FCSTD DOCUMENT  (FreeCAD 1.0R39319 (Git))
Label: Week2Sketch2
License: All rights reserved
LicenseURL: https://en.wikipedia.org/wiki/All_rights_reserved
objects: Spreadsheet::Sheet×1, Sketcher::SketchObject×1, PartDesign::Body×1
note: 3 computed .brp shape members not serialized (recipe doc carries the construction recipe); baked Part::Feature solids carry a one-line shape summary decoded from their .brp

FEATURE [Spreadsheet::Sheet] Spreadsheet
  cells = A1='y_totaldis; B1(y_totaldis)=75; A2='y_rside_max_dis; B2(y_rside_max_dis)=57; A3='right_side_box; B3(right_side_box)=4; A4='y_from_box_to_top; B4(y_from_box_to_top)=14; A5='x_fromrtoptoleft; B5(x_fromrtoptoleft)=18; A6='x_centertop_dis; B6(x_centertop_dis)=22; A7='x_center_box; B7(x_center_box)=8; A8='y_center_box; B8(y_center_box)=4; A9='slant_top_left_dis; B9(slant_top_left_dis)=3; A10='x_dis_from_slant_to_left; B10(x_dis_from_slant_to_left)=21; A11='left_rid ; B11(left_rid)=5; A12='x_disfromlefttoright; B12(x_disfromlefttoright)=5; A13='y_disleftbottom; B13(y_disleftbottom)=10; A14='y_centerdis ; B14(y_centerdis)=22; A15='y_rightbottom; B15(y_rightbottom)=15; A16='x_dis_centerbottom; B16(x_dis_centerbottom)=21; A17='x_dis_rightbottom; B17(x_dis_rightbottom)=17; A18='y_dis_centerbttom; B18(y_dis_centerbttom)=22; A19='x_leftbottom_notch; B19(x_leftbottom_notch)=4; A20='Radius_inner_gear; B20(Radius_inner_gear)=6.4; A21='radius_outer_gear; B21(radius_outer_gear)=8.5; A22='radius_gear; B22(radius_gear)=2.2
FEATURE [Sketcher::SketchObject] Sketch
  ArcFitTolerance = 1e-06
  AttachmentSupport = -> [XY_Plane]
  FullyConstrained = false
  MakeInternals = false
  MapMode = 5
  expr: Constraints[12] = <<Spreadsheet>>.right_side_box
  expr: Constraints[13] = <<Spreadsheet>>.right_side_box
  expr: Constraints[14] = <<Spreadsheet>>.y_from_box_to_top
  expr: Constraints[29] = <<Spreadsheet>>.x_fromrtoptoleft
  expr: Constraints[2] = <<Spreadsheet>>.y_rside_max_dis
  expr: Constraints[30] = <<Spreadsheet>>.y_from_box_to_top + <<Spreadsheet>>.right_side_box
  expr: Constraints[33] = <<Spreadsheet>>.x_centertop_dis
  expr: Constraints[35] = <<Spreadsheet>>.x_center_box
  expr: Constraints[36] = <<Spreadsheet>>.y_center_box
  expr: Constraints[37] = <<Spreadsheet>>.y_from_box_to_top + <<Spreadsheet>>.right_side_box
  expr: Constraints[69] = <<Spreadsheet>>.y_totaldis
  expr: Constraints[70] = <<Spreadsheet>>.slant_top_left_dis
  expr: Constraints[71] = <<Spreadsheet>>.left_rid
  expr: Constraints[72] = <<Spreadsheet>>.x_dis_rightbottom
  expr: Constraints[73] = <<Spreadsheet>>.y_rightbottom
  expr: Constraints[74] = <<Spreadsheet>>.x_dis_centerbottom
  expr: Constraints[75] = <<Spreadsheet>>.y_dis_centerbttom
  expr: Constraints[76] = <<Spreadsheet>>.x_leftbottom_notch
  expr: Constraints[77] = <<Spreadsheet>>.y_disleftbottom
  expr: Constraints[82] = <<Spreadsheet>>.x_dis_from_slant_to_left
  expr: Constraints[83] = <<Spreadsheet>>.x_disfromlefttoright
  expr: Constraints[93] = <<Spreadsheet>>.radius_outer_gear
  expr: Constraints[95] = <<Spreadsheet>>.Radius_inner_gear
  sketch-geometry (55):
    g0: LineSegment StartX=0 StartY=0 StartZ=0 EndX=0 EndY=57 EndZ=0
    g1: LineSegment StartX=0 StartY=57 StartZ=0 EndX=-4 EndY=57 EndZ=0
    g2: LineSegment StartX=-4 StartY=57 StartZ=0 EndX=-4 EndY=61 EndZ=0
    g3: LineSegment StartX=-4 StartY=61 StartZ=0 EndX=0 EndY=61 EndZ=0
    g4: LineSegment StartX=0 StartY=61 StartZ=0 EndX=0 EndY=75 EndZ=0
    g5: LineSegment StartX=0 StartY=75 StartZ=0 EndX=-18 EndY=75 EndZ=0
    g6: LineSegment StartX=-18 StartY=75 StartZ=0 EndX=-18 EndY=57 EndZ=0
    g7: LineSegment StartX=-18 StartY=57 StartZ=0 EndX=-25 EndY=57 EndZ=0
    g8: LineSegment StartX=-25 StartY=57 StartZ=0 EndX=-25 EndY=53 EndZ=0
    g9: LineSegment StartX=-25 StartY=53 StartZ=0 EndX=-33 EndY=53 EndZ=0
    g10: LineSegment StartX=-33 StartY=53 StartZ=0 EndX=-33 EndY=57 EndZ=0
    g11: LineSegment StartX=-33 StartY=57 StartZ=0 EndX=-40 EndY=57 EndZ=0
    g12: LineSegment StartX=-40 StartY=57 StartZ=0 EndX=-40 EndY=73.4506 EndZ=0
    g13: LineSegment StartX=0 StartY=0 StartZ=0 EndX=-17 EndY=0 EndZ=0
    g14: LineSegment StartX=-17 StartY=0 StartZ=0 EndX=-17 EndY=15 EndZ=0
    g15: LineSegment StartX=-17 StartY=15 StartZ=0 EndX=-38 EndY=15 EndZ=0
    g16: LineSegment StartX=-38 StartY=15 StartZ=0 EndX=-38 EndY=37 EndZ=0
    g17: LineSegment StartX=-38 StartY=37 StartZ=0 EndX=-42 EndY=37 EndZ=0
    g18: LineSegment StartX=-42 StartY=37 StartZ=0 EndX=-42 EndY=27 EndZ=0
    g19: LineSegment StartX=-42 StartY=27 StartZ=0 EndX=-46 EndY=27 EndZ=0
    g20: LineSegment StartX=-46 StartY=27 StartZ=0 EndX=-46 EndY=32 EndZ=0
    g21: LineSegment StartX=-46 StartY=32 StartZ=0 EndX=-50 EndY=32 EndZ=0
    g22: LineSegment StartX=-50 StartY=32 StartZ=0 EndX=-50 EndY=27 EndZ=0
    g23: LineSegment StartX=-50 StartY=27 StartZ=0 EndX=-54 EndY=27 EndZ=0
    g24: LineSegment StartX=-54 StartY=27 StartZ=0 EndX=-54 EndY=37 EndZ=0
    g25: LineSegment StartX=-54 StartY=37 StartZ=0 EndX=-59 EndY=37 EndZ=0
    g26: LineSegment StartX=-59 StartY=37 StartZ=0 EndX=-59 EndY=61 EndZ=0
    g27: ArcOfCircle CenterX=-54 CenterY=61 CenterZ=0 NormalX=0 NormalY=0 NormalZ=1 AngleXU=0 Radius=5 StartAngle=2.17657 EndAngle=3.14159
    g28: LineSegment StartX=-56.847 StartY=65.1103 StartZ=0 EndX=-42.5689 EndY=75 EndZ=0
    g29: LineSegment StartX=-42.5689 StartY=75 StartZ=0 EndX=-40 EndY=73.4506 EndZ=0
    g30: GeomPoint X=-54 Y=32 Z=0
    g31: LineSegment [constr] StartX=-38 StartY=37 StartZ=0 EndX=-17 EndY=37 EndZ=0
    g32: LineSegment [constr] StartX=-17 StartY=15 StartZ=0 EndX=-17 EndY=37 EndZ=0
    g33: ArcOfCircle CenterX=-17 CenterY=37 CenterZ=0 NormalX=0 NormalY=0 NormalZ=1 AngleXU=0 Radius=4.25 StartAngle=2.11632 EndAngle=2.25889
    g34: Circle [constr] CenterX=-17 CenterY=37 CenterZ=0 NormalX=0 NormalY=0 NormalZ=1 AngleXU=0 Radius=3.2
    g35: ArcOfCircle CenterX=-21.25 CenterY=37 CenterZ=0 NormalX=0 NormalY=0 NormalZ=1 AngleXU=0 Radius=1.05 StartAngle=4.83623 EndAngle=7.73014
    g36: ArcOfCircle CenterX=-20.4215 CenterY=39.521 CenterZ=0 NormalX=0 NormalY=0 NormalZ=1 AngleXU=0 Radius=1.05 StartAngle=4.20123 EndAngle=7.09513
    g37: ArcOfCircle CenterX=-18.2472 CenterY=41.0629 CenterZ=0 NormalX=0 NormalY=0 NormalZ=1 AngleXU=0 Radius=1.05 StartAngle=3.56327 EndAngle=6.45717
    g38: ArcOfCircle CenterX=-15.6866 CenterY=41.042 CenterZ=0 NormalX=0 NormalY=0 NormalZ=1 AngleXU=0 Radius=1.05 StartAngle=2.95125 EndAngle=5.84515
    g39: ArcOfCircle CenterX=-13.592 CenterY=39.5393 CenterZ=0 NormalX=0 NormalY=0 NormalZ=1 AngleXU=0 Radius=1.05 StartAngle=2.335 EndAngle=5.2289
    g40: ArcOfCircle CenterX=-12.7505 CenterY=37.0661 CenterZ=0 NormalX=0 NormalY=0 NormalZ=1 AngleXU=0 Radius=1.05 StartAngle=1.7102 EndAngle=4.6041
    g41: ArcOfCircle CenterX=-13.5156 CenterY=34.5666 CenterZ=0 NormalX=0 NormalY=0 NormalZ=1 AngleXU=0 Radius=1.05 StartAngle=1.08501 EndAngle=3.97891
    g42: ArcOfCircle CenterX=-15.5707 CenterY=32.9976 CenterZ=0 NormalX=0 NormalY=0 NormalZ=1 AngleXU=0 Radius=1.05 StartAngle=0.46684 EndAngle=3.36074
    g43: ArcOfCircle CenterX=-18.329 CenterY=32.9631 CenterZ=0 NormalX=0 NormalY=0 NormalZ=1 AngleXU=0 Radius=1.05 StartAngle=6.089 EndAngle=8.9829
    g44: ArcOfCircle CenterX=-20.3699 CenterY=34.4104 CenterZ=0 NormalX=0 NormalY=0 NormalZ=1 AngleXU=0 Radius=1.05 StartAngle=5.49145 EndAngle=8.38535
    g45: ArcOfCircle CenterX=-21.25 CenterY=37 CenterZ=0 NormalX=0 NormalY=0 NormalZ=1 AngleXU=0 Radius=1.05 StartAngle=4.83624 EndAngle=7.73014
    g46: ArcOfCircle CenterX=-17 CenterY=37 CenterZ=0 NormalX=0 NormalY=0 NormalZ=1 AngleXU=0 Radius=4.25 StartAngle=1.5043 EndAngle=1.62094
    g47: ArcOfCircle CenterX=-17 CenterY=37 CenterZ=0 NormalX=0 NormalY=0 NormalZ=1 AngleXU=0 Radius=4.25 StartAngle=0.888051 EndAngle=1.00892
    g48: ArcOfCircle CenterX=-17 CenterY=37 CenterZ=0 NormalX=0 NormalY=0 NormalZ=1 AngleXU=0 Radius=4.25 StartAngle=0.263249 EndAngle=0.392668
    g49: ArcOfCircle CenterX=-17 CenterY=37 CenterZ=0 NormalX=0 NormalY=0 NormalZ=1 AngleXU=0 Radius=4.25 StartAngle=5.92124 EndAngle=6.05105
    g50: ArcOfCircle CenterX=-17 CenterY=37 CenterZ=0 NormalX=0 NormalY=0 NormalZ=1 AngleXU=0 Radius=4.25 StartAngle=5.30307 EndAngle=5.42586
    g51: ArcOfCircle CenterX=-17 CenterY=37 CenterZ=0 NormalX=0 NormalY=0 NormalZ=1 AngleXU=0 Radius=4.25 StartAngle=4.64205 EndAngle=4.80769
    g52: ArcOfCircle CenterX=-17 CenterY=37 CenterZ=0 NormalX=0 NormalY=0 NormalZ=1 AngleXU=0 Radius=4.25 StartAngle=4.0445 EndAngle=4.14666
    g53: ArcOfCircle CenterX=-17 CenterY=37 CenterZ=0 NormalX=0 NormalY=0 NormalZ=1 AngleXU=0 Radius=4.25 StartAngle=3.38928 EndAngle=3.54911
    g54: ArcOfCircle CenterX=-17 CenterY=37 CenterZ=0 NormalX=0 NormalY=0 NormalZ=1 AngleXU=0 Radius=4.25 StartAngle=2.75427 EndAngle=2.8939
  constraints (160):
    c: Coincident(g0,g-1)
    c: PointOnObject(g0,g-2)
    c: DistanceY(g0,g0) = 57
    c: Coincident(g0,g1)
    c: Horizontal(g1)
    c: Coincident(g1,g2)
    c: Vertical(g2)
    c: Coincident(g2,g3)
    c: PointOnObject(g3,g-2)
    c: Horizontal(g3)
    c: Coincident(g3,g4)
    c: PointOnObject(g4,g-2)
    c: Distance(g1,g1) = 4
    c: DistanceY(g2,g2) = 4
    c: DistanceY(g4,g4) = 14
    c: Coincident(g4,g5)
    c: Horizontal(g5)
    c: Coincident(g5,g6)
    c: Vertical(g6)
    c: Coincident(g6,g7)
    c: Horizontal(g7)
    c: Coincident(g7,g8)
    c: Vertical(g8)
    c: Coincident(g8,g9)
    c: Horizontal(g9)
    c: Coincident(g9,g10)
    c: Vertical(g10)
    c: Coincident(g10,g11)
    c: Horizontal(g11)
    c: DistanceX(g5,g5) = 18
    c: DistanceY(g6,g6) = 18
    c: Coincident(g12,g11)
    c: Vertical(g12)
    c: Distance(g12,g6) = 22
    c: Equal(g7,g11)
    c: DistanceX(g9,g9) = 8
    c: Distance(g11,g9) = 4
    c: Distance(g11,g5) = 18
    c: Coincident(g0,g13)
    c: PointOnObject(g13,g-1)
    c: Coincident(g13,g14)
    c: Vertical(g14)
    c: Coincident(g14,g15)
    c: Horizontal(g15)
    c: Coincident(g15,g16)
    c: Vertical(g16)
    c: Coincident(g16,g17)
    c: Horizontal(g17)
    c: Coincident(g17,g18)
    c: Vertical(g18)
    c: Coincident(g18,g19)
    c: Horizontal(g19)
    c: Coincident(g19,g20)
    c: Coincident(g20,g21)
    c: Horizontal(g21)
    c: Coincident(g21,g22)
    c: Vertical(g22)
    c: Coincident(g22,g23)
    c: Horizontal(g23)
    c: Coincident(g23,g24)
    c: Vertical(g24)
    c: Coincident(g24,g25)
    c: Horizontal(g25)
    c: Coincident(g25,g26)
    c: Vertical(g26)
    c: Tangent(g26,g27) = 1.5708
    c: Tangent(g27,g28) = 1.5708
    c: Coincident(g28,g29)
    c: Coincident(g29,g12)
    c: Distance(g28,g13) = 75
    c: Distance(g29,g29) = 3
    c: Radius(g27) = 5
    c: DistanceX(g13,g13) = 17
    c: DistanceY(g14,g14) = 15
    c: DistanceX(g15,g15) = 21
    c: DistanceY(g16,g16) = 22
    c: Distance(g17,g17) = 4
    c: DistanceY(g18,g18) = 10
    c: Vertical(g20)
    c: Equal(g18,g24)
    c: Equal(g23,g21)
    c: Equal(g21,g19)
    c: Distance(g26,g16) = 21
    c: Distance(g25,g25) = 5
    c: Equal(g20,g22)
    c: Symmetric(g24,g24,g30)
    c: Horizontal(g21,g30)
    c: Coincident(g31,g16)
    c: Horizontal(g31)
    c: Coincident(g32,g14)
    c: Vertical(g32)
    c: Coincident(g31,g32)
    c: Coincident(g33,g31)
    c: Diameter(g33) = 8.5
    c: Coincident(g34,g31)
    c: Diameter(g34) = 6.4
    c: Block(g32)
    c: Block(g31)
    c: PointOnObject(g35,g31)
    c: Tangent(g35,g34)
    c: PointOnObject(g35,g53)
    c: PointOnObject(g35,g54)
    c: PointOnObject(g36,g54)
    c: PointOnObject(g36,g33)
    c: PointOnObject(g37,g33)
    c: PointOnObject(g38,g46)
    c: PointOnObject(g38,g33)
    c: PointOnObject(g39,g47)
    c: PointOnObject(g39,g33)
    c: PointOnObject(g40,g48)
    c: PointOnObject(g40,g33)
    c: PointOnObject(g41,g49)
    c: PointOnObject(g41,g33)
    c: PointOnObject(g42,g50)
    c: PointOnObject(g42,g51)
    c: PointOnObject(g43,g51)
    c: PointOnObject(g43,g52)
    c: PointOnObject(g44,g52)
    c: PointOnObject(g44,g53)
    c: Equal(g35, g36-g44) x9
    c: Coincident(g46,g37)
    c: Coincident(g33,g37)
    c: Equal(g33,g46)
    c: Coincident(g47,g38)
    c: PointOnObject(g46,g38)
    c: Coincident(g33,g46)
    c: Equal(g33,g47)
    c: Coincident(g48,g39)
    c: PointOnObject(g47,g39)
    c: Coincident(g33,g47)
    c: Equal(g33,g48)
    c: Coincident(g49,g40)
    c: PointOnObject(g48,g40)
    c: Coincident(g33,g48)
    c: Equal(g33,g49)
    c: Coincident(g50,g41)
    c: PointOnObject(g49,g41)
    c: Coincident(g33,g49)
    c: Equal(g33,g50)
    c: Coincident(g51,g42)
    c: PointOnObject(g50,g42)
    c: Coincident(g33,g50)
    c: Equal(g33,g51)
    c: Coincident(g52,g43)
    c: PointOnObject(g51,g43)
    c: Coincident(g33,g51)
    c: Equal(g33,g52)
    c: Coincident(g53,g44)
    c: PointOnObject(g52,g44)
    c: Coincident(g33,g52)
    c: Equal(g33,g53)
    c: PointOnObject(g53,g35)
    c: Coincident(g33,g53)
    c: Coincident(g54,g35)
    c: Equal(g33,g54)
    c: Coincident(g33,g36)
    c: PointOnObject(g54,g36)
    c: Coincident(g33,g54)
    c: DistanceY(g26,g28) = 14
    c: Block(g29)
FEATURE [PartDesign::Body] Body
  AllowCompound = false
  Group = -> [Sketch]
  Origin = -> Origin
